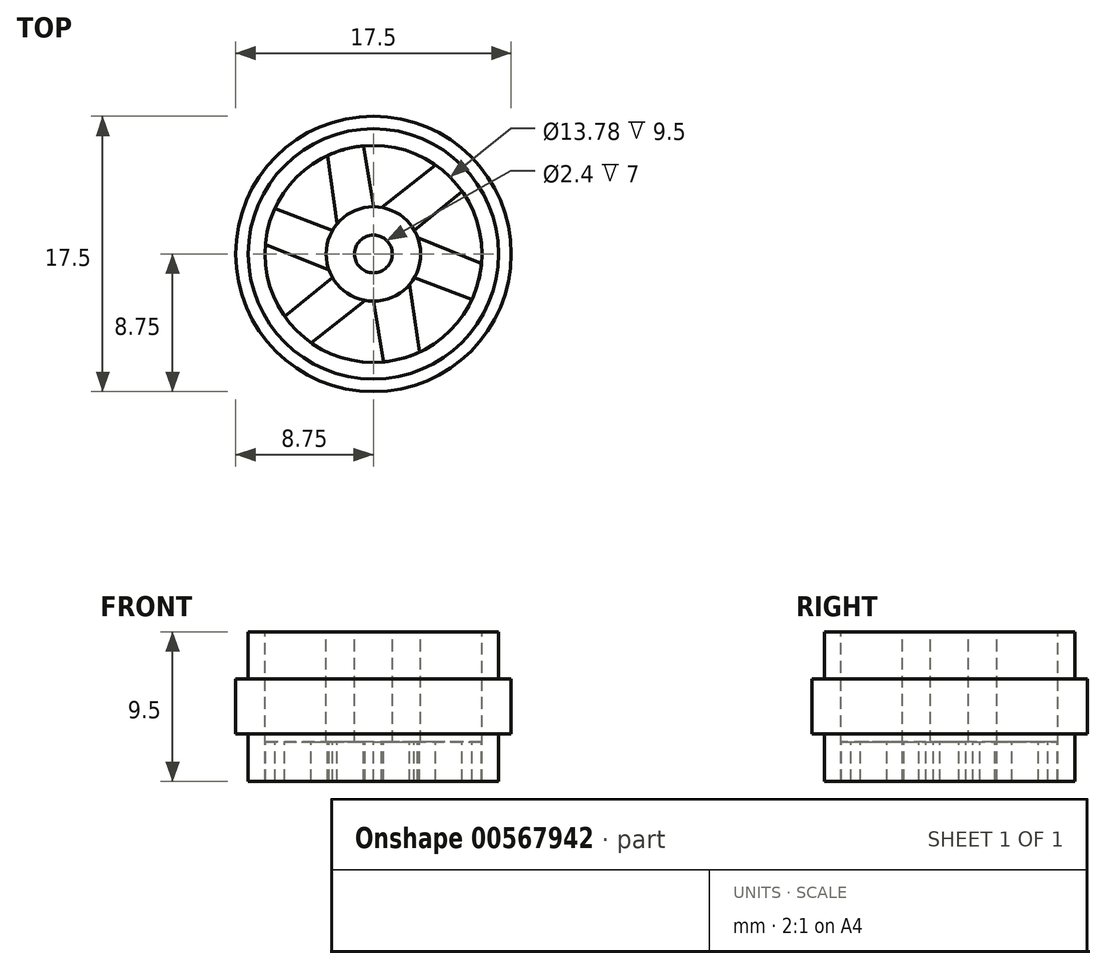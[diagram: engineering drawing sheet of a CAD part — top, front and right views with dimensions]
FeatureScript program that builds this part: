
annotation { "Feature Type Name" : "Feature", "Feature Type Description" : "" }
export const myFeature = defineFeature(function(context is Context, id is Id, definition is map)
    precondition{}
    {
        {
            var Q0;
            Q0=qCreatedBy(makeId("Top.planeOp"),FACE);
            var sketch = newSketch(context, id + "F0", { "sketchPlane" : qUnion([Q0])});
            skCircle(sketch, "E0", {"center": v(0, 0) * mm, "radius": 7.95 * mm});
            skSolve(sketch);
        }
        {
            var Q0;
            Q0=makeQuery(id+"F0.imprint","IMPRINT",FACE,{"disambiguationData":[TD([[makeQuery(id+"F0.imprint","IMPRINT",EDGE,{"derivedFrom":sQuery(id+"F0.wireOp",EDGE,"E0")}),1.0]])]});
            extrude(context, id + "F1", {"entities" : qUnion([Q0]), "depth" : 3 * mm, "offsetDistance" : 25 * mm});
        }
        {
            var Q0;
            Q0=makeQuery(id+"F1.opExtrude","CAP_FACE",FACE,{"disambiguationData":[OSD([sQuery(id+"F0.wireOp",EDGE,"E0")])],"isStart":false});
            var sketch = newSketch(context, id + "F2", { "sketchPlane" : qUnion([Q0])});
            skCircle(sketch, "E1", {"center": v(0, 0) * mm, "radius": 8.75 * mm});
            skSolve(sketch);
        }
        {
            var Q0;
            Q0 = qSketchRegion(id + "F2", true);
            extrude(context, id + "F3", {"entities" : qUnion([Q0]), "operationType" : NewBodyOperationType.ADD, "depth" : 3.5 * mm, "offsetDistance" : 25 * mm});
        }
        {
            var Q0;
            Q0=makeQuery(id+"F3.opExtrude","CAP_FACE",FACE,{"disambiguationData":[OSD([sQuery(id+"F2.wireOp",EDGE,"E1")])],"isStart":false});
            var sketch = newSketch(context, id + "F4", { "sketchPlane" : qUnion([Q0])});
            skCircle(sketch, "E2", {"center": v(0, 0) * mm, "radius": 7.95 * mm});
            skSolve(sketch);
        }
        {
            var Q0;
            Q0 = qSketchRegion(id + "F4", true);
            extrude(context, id + "F5", {"entities" : qUnion([Q0]), "operationType" : NewBodyOperationType.ADD, "depth" : 3 * mm, "offsetDistance" : 25 * mm});
        }
        {
            var Q0;
            Q0=makeQuery(id+"F5.opExtrude","CAP_FACE",FACE,{"disambiguationData":[OSD([sQuery(id+"F4.wireOp",EDGE,"E2")])],"isStart":false});
            var sketch = newSketch(context, id + "F6", { "sketchPlane" : qUnion([Q0])});
            skCircle(sketch, "E3", {"center": v(0, 0) * mm, "radius": 1.2 * mm});
            skCircle(sketch, "E4", {"center": v(0, 0) * mm, "radius": 3 * mm});
            skLineSegment(sketch, "E5", {"start": v(-3.95, -5.65) * mm, "end": v(-0.52, -2.95) * mm});
            skLineSegment(sketch, "E6", {"start": v(0, -3) * mm, "end": v(0.63, -6.86) * mm});
            skLineSegment(sketch, "E7.1.0", {"start": v(2.6, -1.5) * mm, "end": v(6.26, -2.89) * mm});
            skLineSegment(sketch, "E7.1.1", {"start": v(2.92, -6.24) * mm, "end": v(2.3, -1.93) * mm});
            skLineSegment(sketch, "E7.2.0", {"start": v(2.6, 1.5) * mm, "end": v(5.63, 3.98) * mm});
            skLineSegment(sketch, "E7.2.1", {"start": v(6.86, -0.6) * mm, "end": v(2.82, 1.03) * mm});
            skLineSegment(sketch, "E7.3.0", {"start": v(0, 3) * mm, "end": v(-0.63, 6.86) * mm});
            skLineSegment(sketch, "E7.3.1", {"start": v(3.95, 5.65) * mm, "end": v(0.52, 2.95) * mm});
            skLineSegment(sketch, "E7.4.0", {"start": v(-2.6, 1.5) * mm, "end": v(-6.26, 2.89) * mm});
            skLineSegment(sketch, "E7.4.1", {"start": v(-2.92, 6.24) * mm, "end": v(-2.3, 1.93) * mm});
            skLineSegment(sketch, "E7.5.0", {"start": v(-2.6, -1.5) * mm, "end": v(-5.63, -3.98) * mm});
            skLineSegment(sketch, "E7.5.1", {"start": v(-6.86, 0.6) * mm, "end": v(-2.82, -1.03) * mm});
            skCircle(sketch, "E8", {"center": v(0, 0) * mm, "radius": 6.9 * mm});
            skPoint(sketch, "E9.orphan", {"position": v(-3.07, 7.33) * mm});
            skPoint(sketch, "E10.orphan", {"position": v(-0.8, 7.9) * mm});
            skPoint(sketch, "E11.orphan", {"position": v(4.82, 6.33) * mm});
            skPoint(sketch, "E12.orphan", {"position": v(6.45, 4.65) * mm});
            skPoint(sketch, "E13.orphan", {"position": v(7.89, -1) * mm});
            skPoint(sketch, "E14.orphan", {"position": v(7.25, -3.26) * mm});
            skPoint(sketch, "E15.orphan", {"position": v(3.07, -7.33) * mm});
            skPoint(sketch, "E16.orphan", {"position": v(0.8, -7.9) * mm});
            skPoint(sketch, "E17.orphan", {"position": v(-4.82, -6.33) * mm});
            skPoint(sketch, "E18.orphan", {"position": v(-6.45, -4.65) * mm});
            skPoint(sketch, "E19.orphan", {"position": v(-7.89, 1) * mm});
            skPoint(sketch, "E20.orphan", {"position": v(-7.25, 3.26) * mm});
            skSolve(sketch);
        }
        {
            var Q0;
            {var subQ0=sQuery(id+"F6.wireOp",EDGE,"E7.4.0");Q0=makeQuery(id+"F6.imprint","IMPRINT",FACE,{"disambiguationData":[TD([[makeQuery(id+"F6.imprint","IMPRINT",EDGE,{"derivedFrom":subQ0}),-1.0]])]});}
            var Q1;
            {var subQ0=sQuery(id+"F6.wireOp",EDGE,"E7.3.0");Q1=makeQuery(id+"F6.imprint","IMPRINT",FACE,{"disambiguationData":[TD([[makeQuery(id+"F6.imprint","IMPRINT",EDGE,{"derivedFrom":subQ0}),-1.0]])]});}
            var Q2;
            {var subQ0=sQuery(id+"F6.wireOp",EDGE,"E7.2.0");Q2=makeQuery(id+"F6.imprint","IMPRINT",FACE,{"disambiguationData":[TD([[makeQuery(id+"F6.imprint","IMPRINT",EDGE,{"derivedFrom":subQ0}),-1.0]])]});}
            var Q3;
            {var subQ0=sQuery(id+"F6.wireOp",EDGE,"E7.1.0");Q3=makeQuery(id+"F6.imprint","IMPRINT",FACE,{"disambiguationData":[TD([[makeQuery(id+"F6.imprint","IMPRINT",EDGE,{"derivedFrom":subQ0}),-1.0]])]});}
            var Q4;
            {var subQ0=sQuery(id+"F6.wireOp",EDGE,"E5");Q4=makeQuery(id+"F6.imprint","IMPRINT",FACE,{"disambiguationData":[TD([[makeQuery(id+"F6.imprint","IMPRINT",EDGE,{"derivedFrom":subQ0}),-1.0]])]});}
            var Q5;
            {var subQ0=sQuery(id+"F6.wireOp",EDGE,"E7.5.0");Q5=makeQuery(id+"F6.imprint","IMPRINT",FACE,{"disambiguationData":[TD([[makeQuery(id+"F6.imprint","IMPRINT",EDGE,{"derivedFrom":subQ0}),-1.0]])]});}
            extrude(context, id + "F7", {"entities" : qUnion([Q0, Q1, Q2, Q3, Q4, Q5]), "operationType" : NewBodyOperationType.REMOVE, "oppositeDirection" : true, "depth" : 25 * mm, "offsetDistance" : 25 * mm});
        }
        {
            var Q0;
            Q0=makeQuery(id+"F6.imprint","IMPRINT",FACE,{"disambiguationData":[TD([[makeQuery(id+"F6.imprint","IMPRINT",EDGE,{"derivedFrom":sQuery(id+"F6.wireOp",EDGE,"E3")}),1.0]])]});
            var Q1;
            {var subQ0=sQuery(id+"F6.wireOp",EDGE,"E7.4.0");Q1=makeQuery(id+"F6.imprint","IMPRINT",FACE,{"disambiguationData":[TD([[makeQuery(id+"F6.imprint","IMPRINT",EDGE,{"derivedFrom":subQ0}),1.0]])]});}
            var Q2;
            {var subQ0=sQuery(id+"F6.wireOp",EDGE,"E7.3.0");Q2=makeQuery(id+"F6.imprint","IMPRINT",FACE,{"disambiguationData":[TD([[makeQuery(id+"F6.imprint","IMPRINT",EDGE,{"derivedFrom":subQ0}),1.0]])]});}
            var Q3;
            {var subQ0=sQuery(id+"F6.wireOp",EDGE,"E7.2.0");Q3=makeQuery(id+"F6.imprint","IMPRINT",FACE,{"disambiguationData":[TD([[makeQuery(id+"F6.imprint","IMPRINT",EDGE,{"derivedFrom":subQ0}),1.0]])]});}
            var Q4;
            {var subQ0=sQuery(id+"F6.wireOp",EDGE,"E7.1.0");Q4=makeQuery(id+"F6.imprint","IMPRINT",FACE,{"disambiguationData":[TD([[makeQuery(id+"F6.imprint","IMPRINT",EDGE,{"derivedFrom":subQ0}),1.0]])]});}
            var Q5;
            {var subQ0=sQuery(id+"F6.wireOp",EDGE,"E6");Q5=makeQuery(id+"F6.imprint","IMPRINT",FACE,{"disambiguationData":[TD([[makeQuery(id+"F6.imprint","IMPRINT",EDGE,{"derivedFrom":subQ0}),1.0]])]});}
            var Q6;
            {var subQ0=sQuery(id+"F6.wireOp",EDGE,"E5");Q6=makeQuery(id+"F6.imprint","IMPRINT",FACE,{"disambiguationData":[TD([[makeQuery(id+"F6.imprint","IMPRINT",EDGE,{"derivedFrom":subQ0}),1.0]])]});}
            extrude(context, id + "F8", {"entities" : qUnion([Q0, Q1, Q2, Q3, Q4, Q5, Q6]), "operationType" : NewBodyOperationType.REMOVE, "oppositeDirection" : true, "depth" : 7 * mm, "offsetDistance" : 25 * mm});
        }
    });
